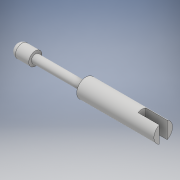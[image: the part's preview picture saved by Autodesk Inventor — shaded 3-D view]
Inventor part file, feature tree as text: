
AUTODESK INVENTOR PART (.ipt)
format: ipt  version: 2017 (Build 210142000, 142)  size: 124,416 bytes
history: native  units: mm
features: extrude x4, sketch x4, fillet x1
ambient origin geometry x8: Origin, YZ Plane, XZ Plane, XY Plane, X Axis, Y Axis, Z Axis, Center Point
bodies: Solid1 (feature_tree)
feature tree (9):
  extrude  "Extrusion1"  Depth=29.0mm TaperAngle=0.0deg
  extrude  "Extrusion2"  Depth=3.0mm
  extrude  "Extrusion3"  Depth=3.0mm
  extrude  "Extrusion4"  Depth=2.0mm
  fillet  "Fillet1"  Radius=7.0mm
  sketch  "Sketch1"  dims[d0=7.0mm d1=29.0mm d2=0.0mm]
  sketch  "Sketch2"  dims[d3=10.0mm d4=3.0mm]
  sketch  "Sketch3"  dims[d5=8.0mm d6=0.0mm d7=3.0mm]
  sketch  "Sketch4"  dims[d8=26.0mm d9=0.0mm d10=5.0mm d11=7.0mm d12=0.0mm d13=2.0mm]
